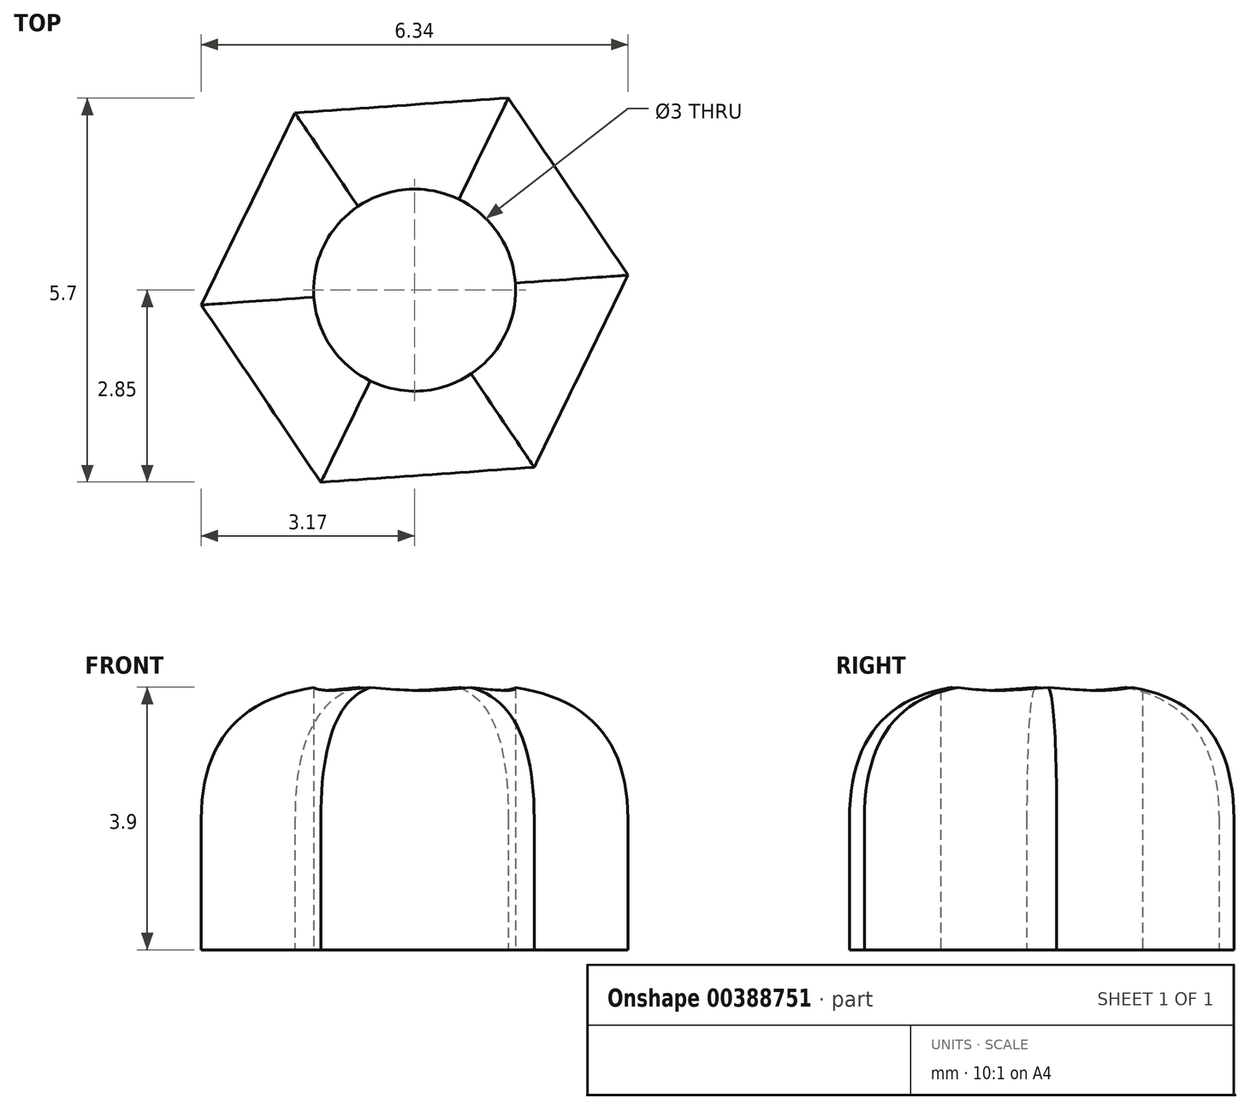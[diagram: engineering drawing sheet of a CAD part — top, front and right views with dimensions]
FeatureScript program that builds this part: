
annotation { "Feature Type Name" : "Feature", "Feature Type Description" : "" }
export const myFeature = defineFeature(function(context is Context, id is Id, definition is map)
    precondition{}
    {
        {
            var Q0;
            Q0=qCreatedBy(makeId("Top.planeOp"),FACE);
            var sketch = newSketch(context, id + "F0", { "sketchPlane" : qUnion([Q0])});
            skCircle(sketch, "E0.cCircle", {"center": v(0, 0) * mm, "radius": 2.75 * mm, "construction": true});
            skLineSegment(sketch, "E0.0", {"start": v(3.17, 0.22) * mm, "end": v(1.78, -2.63) * mm});
            skLineSegment(sketch, "E0.1", {"start": v(1.78, -2.63) * mm, "end": v(-1.4, -2.85) * mm});
            skLineSegment(sketch, "E0.2", {"start": v(-1.4, -2.85) * mm, "end": v(-3.17, -0.22) * mm});
            skLineSegment(sketch, "E0.3", {"start": v(-3.17, -0.22) * mm, "end": v(-1.78, 2.63) * mm});
            skLineSegment(sketch, "E0.4", {"start": v(-1.78, 2.63) * mm, "end": v(1.4, 2.85) * mm});
            skLineSegment(sketch, "E0.5", {"start": v(1.4, 2.85) * mm, "end": v(3.17, 0.22) * mm});
            skPoint(sketch, "E0.0.midPoint", {"position": v(2.47, -1.2) * mm});
            skCircle(sketch, "E1", {"center": v(0, 0) * mm, "radius": 1.5 * mm});
            skSolve(sketch);
        }
        {
            var Q0;
            Q0=makeQuery(id+"F0.imprint","IMPRINT",FACE,{"disambiguationData":[TD([[makeQuery(id+"F0.imprint","IMPRINT",EDGE,{"derivedFrom":sQuery(id+"F0.wireOp",EDGE,"E0.0")}),-1.0]])]});
            extrude(context, id + "F1", {"entities" : qUnion([Q0]), "depth" : 3.94 * mm});
        }
        {
            var Q0;
            Q0=makeQuery(id+"F1.opExtrude","CAP_EDGE",EDGE,{"disambiguationData":[OSD([sQuery(id+"F0.wireOp",EDGE,"E0.2")])],"isStart":false});
            var Q1;
            Q1=makeQuery(id+"F1.opExtrude","CAP_EDGE",EDGE,{"disambiguationData":[OSD([sQuery(id+"F0.wireOp",EDGE,"E0.3")])],"isStart":false});
            var Q2;
            Q2=makeQuery(id+"F1.opExtrude","CAP_EDGE",EDGE,{"disambiguationData":[OSD([sQuery(id+"F0.wireOp",EDGE,"E0.4")])],"isStart":false});
            var Q3;
            Q3=makeQuery(id+"F1.opExtrude","CAP_EDGE",EDGE,{"disambiguationData":[OSD([sQuery(id+"F0.wireOp",EDGE,"E0.5")])],"isStart":false});
            var Q4;
            Q4=makeQuery(id+"F1.opExtrude","CAP_EDGE",EDGE,{"disambiguationData":[OSD([sQuery(id+"F0.wireOp",EDGE,"E0.0")])],"isStart":false});
            var Q5;
            Q5=makeQuery(id+"F1.opExtrude","CAP_EDGE",EDGE,{"disambiguationData":[OSD([sQuery(id+"F0.wireOp",EDGE,"E0.1")])],"isStart":false});
            fillet(context, id + "F2", {"entities" : qUnion([Q0, Q1, Q2, Q3, Q4, Q5]), "radius" : 2 * mm, "tangentPropagation" : true, "rho" : 0.5, "crossSection" : FilletCrossSection.CONIC, "allowEdgeOverflow" : false});
        }
    });
